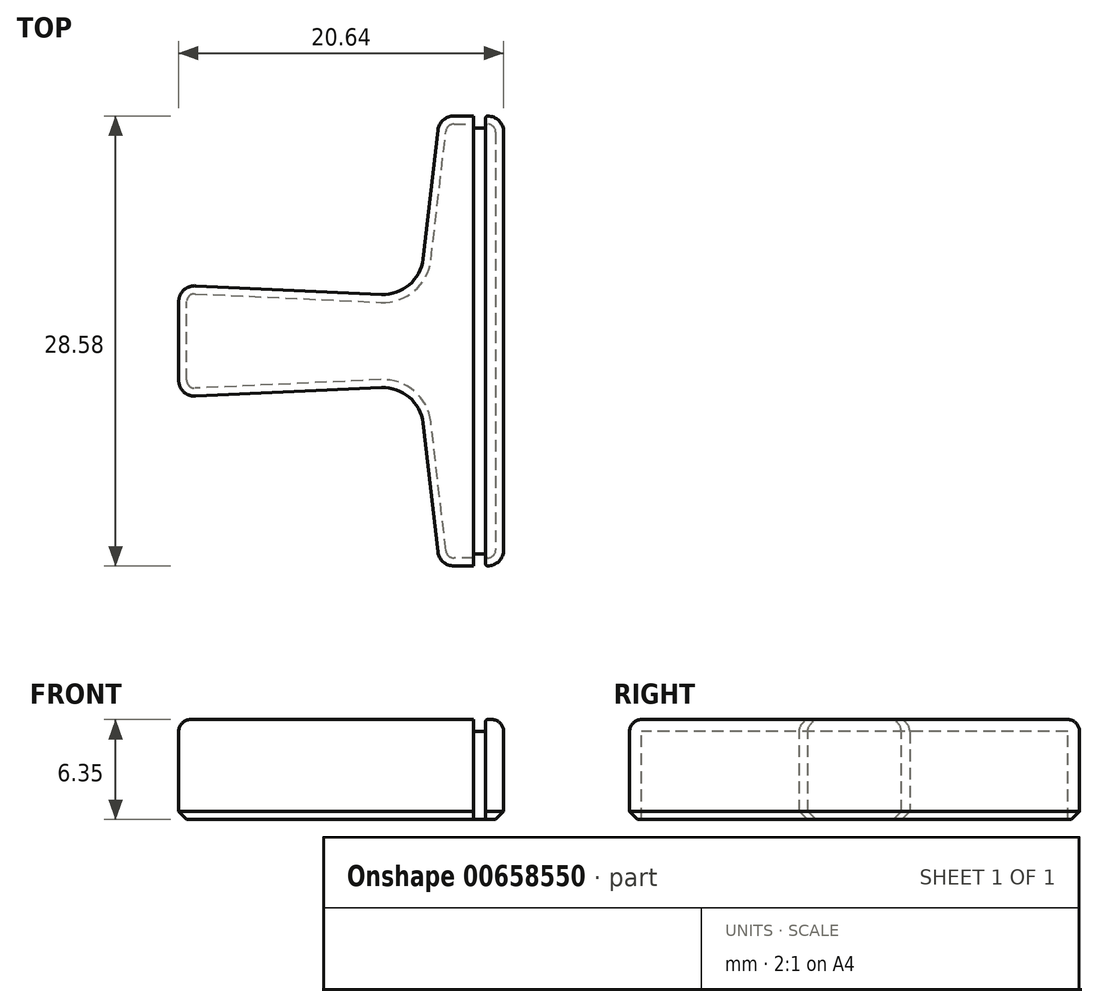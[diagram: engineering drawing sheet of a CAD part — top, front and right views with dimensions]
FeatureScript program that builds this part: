
annotation { "Feature Type Name" : "Feature", "Feature Type Description" : "" }
export const myFeature = defineFeature(function(context is Context, id is Id, definition is map)
    precondition{}
    {
        {
            var Q0;
            Q0=qCreatedBy(makeId("Top.planeOp"),FACE);
            var sketch = newSketch(context, id + "F0", { "sketchPlane" : qUnion([Q0])});
            skLineSegment(sketch, "E0", {"start": v(0, 14.29) * mm, "end": v(0, -14.29) * mm});
            skLineSegment(sketch, "E1", {"start": v(-20.64, 3.56) * mm, "end": v(-20.64, -3.56) * mm});
            skLineSegment(sketch, "E2", {"start": v(0, 14.29) * mm, "end": v(-4.06, 14.29) * mm});
            skLineSegment(sketch, "E3", {"start": v(-4.06, 14.29) * mm, "end": v(-5.4, 2.86) * mm});
            skLineSegment(sketch, "E4", {"start": v(-5.4, 2.86) * mm, "end": v(-20.64, 3.56) * mm});
            skLineSegment(sketch, "E5", {"start": v(0, -14.29) * mm, "end": v(-4.06, -14.29) * mm});
            skLineSegment(sketch, "E6", {"start": v(-4.06, -14.29) * mm, "end": v(-5.4, -2.86) * mm});
            skLineSegment(sketch, "E7", {"start": v(-5.4, -2.86) * mm, "end": v(-20.64, -3.56) * mm});
            skSolve(sketch);
        }
        {
            var Q0;
            Q0 = qSketchRegion(id + "F0", true);
            extrude(context, id + "F1", {"entities" : qUnion([Q0]), "depth" : 6.35 * mm, "offsetDistance" : 25.4 * mm});
        }
        {
            var Q0;
            Q0=makeQuery(id+"F1.opExtrude","SWEPT_EDGE",EDGE,{"disambiguationData":[OSD([sQuery(id+"F0.wireOp",EDGE,"E6"),sQuery(id+"F0.wireOp",EDGE,"E7")])]});
            var Q1;
            Q1=makeQuery(id+"F1.opExtrude","SWEPT_EDGE",EDGE,{"disambiguationData":[OSD([sQuery(id+"F0.wireOp",EDGE,"E3"),sQuery(id+"F0.wireOp",EDGE,"E4")])]});
            fillet(context, id + "F2", {"entities" : qUnion([Q0, Q1]), "radius" : 2.54 * mm, "tangentPropagation" : true, "allowEdgeOverflow" : false});
        }
        {
            var Q0;
            Q0=makeQuery(id+"F1.opExtrude","SWEPT_EDGE",EDGE,{"disambiguationData":[OSD([sQuery(id+"F0.wireOp",EDGE,"E0"),sQuery(id+"F0.wireOp",EDGE,"E2")])]});
            var Q1;
            Q1=makeQuery(id+"F1.opExtrude","SWEPT_EDGE",EDGE,{"disambiguationData":[OSD([sQuery(id+"F0.wireOp",EDGE,"E2"),sQuery(id+"F0.wireOp",EDGE,"E3")])]});
            var Q2;
            Q2=makeQuery(id+"F1.opExtrude","SWEPT_EDGE",EDGE,{"disambiguationData":[OSD([sQuery(id+"F0.wireOp",EDGE,"E0"),sQuery(id+"F0.wireOp",EDGE,"E5")])]});
            var Q3;
            Q3=makeQuery(id+"F1.opExtrude","SWEPT_EDGE",EDGE,{"disambiguationData":[OSD([sQuery(id+"F0.wireOp",EDGE,"E5"),sQuery(id+"F0.wireOp",EDGE,"E6")])]});
            var Q4;
            Q4=makeQuery(id+"F1.opExtrude","SWEPT_EDGE",EDGE,{"disambiguationData":[OSD([sQuery(id+"F0.wireOp",EDGE,"E1"),sQuery(id+"F0.wireOp",EDGE,"E4")])]});
            var Q5;
            Q5=makeQuery(id+"F1.opExtrude","SWEPT_EDGE",EDGE,{"disambiguationData":[OSD([sQuery(id+"F0.wireOp",EDGE,"E1"),sQuery(id+"F0.wireOp",EDGE,"E7")])]});
            fillet(context, id + "F3", {"entities" : qUnion([Q0, Q1, Q2, Q3, Q4, Q5]), "radius" : 1.02 * mm, "tangentPropagation" : true, "allowEdgeOverflow" : false});
        }
        {
            var Q0;
            Q0=makeQuery(id+"F1.opExtrude","CAP_FACE",FACE,{"disambiguationData":[OSD([sQuery(id+"F0.wireOp",EDGE,"E0"),sQuery(id+"F0.wireOp",EDGE,"E1"),sQuery(id+"F0.wireOp",EDGE,"E2"),sQuery(id+"F0.wireOp",EDGE,"E3"),sQuery(id+"F0.wireOp",EDGE,"E4"),sQuery(id+"F0.wireOp",EDGE,"E5"),sQuery(id+"F0.wireOp",EDGE,"E6"),sQuery(id+"F0.wireOp",EDGE,"E7")])],"isStart":false});
            fillet(context, id + "F4", {"entities" : qUnion([Q0]), "radius" : 0.76 * mm, "tangentPropagation" : true, "allowEdgeOverflow" : false});
        }
        {
            var Q0;
            Q0=makeQuery(id+"F1.opExtrude","CAP_FACE",FACE,{"disambiguationData":[OSD([sQuery(id+"F0.wireOp",EDGE,"E0"),sQuery(id+"F0.wireOp",EDGE,"E1"),sQuery(id+"F0.wireOp",EDGE,"E2"),sQuery(id+"F0.wireOp",EDGE,"E3"),sQuery(id+"F0.wireOp",EDGE,"E4"),sQuery(id+"F0.wireOp",EDGE,"E5"),sQuery(id+"F0.wireOp",EDGE,"E6"),sQuery(id+"F0.wireOp",EDGE,"E7")])],"isStart":true});
            chamfer(context, id + "F5", {"entities" : qUnion([Q0]), "width" : 0.5 * mm, "tangentPropagation" : true});
        }
        {
            var Q0;
            Q0=makeQuery(id+"F1.opExtrude","CAP_FACE",FACE,{"disambiguationData":[OSD([sQuery(id+"F0.wireOp",EDGE,"E0"),sQuery(id+"F0.wireOp",EDGE,"E1"),sQuery(id+"F0.wireOp",EDGE,"E2"),sQuery(id+"F0.wireOp",EDGE,"E3"),sQuery(id+"F0.wireOp",EDGE,"E4"),sQuery(id+"F0.wireOp",EDGE,"E5"),sQuery(id+"F0.wireOp",EDGE,"E6"),sQuery(id+"F0.wireOp",EDGE,"E7")])],"isStart":false});
            var sketch = newSketch(context, id + "F6", { "sketchPlane" : qUnion([Q0])});
            skLineSegment(sketch, "E8.bottom", {"start": v(-1.9, 15.3) * mm, "end": v(-1.14, 15.3) * mm});
            skLineSegment(sketch, "E8.top", {"start": v(-1.9, -16.46) * mm, "end": v(-1.14, -16.46) * mm});
            skLineSegment(sketch, "E8.left", {"start": v(-1.9, 15.3) * mm, "end": v(-1.9, -16.46) * mm});
            skLineSegment(sketch, "E8.right", {"start": v(-1.14, 15.3) * mm, "end": v(-1.14, -16.46) * mm});
            skSolve(sketch);
        }
        {
            var Q0;
            Q0 = qSketchRegion(id + "F6", true);
            extrude(context, id + "F7", {"entities" : qUnion([Q0]), "operationType" : NewBodyOperationType.REMOVE, "oppositeDirection" : true, "depth" : 0.76 * mm, "offsetDistance" : 25.4 * mm});
        }
        {
            var Q0;
            Q0=makeQuery(id+"F7.boolean.opBoolean","COPY",FACE,{"derivedFrom":makeQuery(id+"F7.opExtrude","CAP_FACE",FACE,{"disambiguationData":[OSD([sQuery(id+"F6.wireOp",EDGE,"E8.bottom"),sQuery(id+"F6.wireOp",EDGE,"E8.top"),sQuery(id+"F6.wireOp",EDGE,"E8.left"),sQuery(id+"F6.wireOp",EDGE,"E8.right")])],"isStart":false})});
            var sketch = newSketch(context, id + "F8", { "sketchPlane" : qUnion([Q0])});
            skLineSegment(sketch, "E9.bottom", {"start": v(-1.9, 14.29) * mm, "end": v(-1.14, 14.29) * mm});
            skLineSegment(sketch, "E9.top", {"start": v(-1.9, 13.54) * mm, "end": v(-1.14, 13.54) * mm});
            skLineSegment(sketch, "E9.left", {"start": v(-1.9, 14.29) * mm, "end": v(-1.9, 13.54) * mm});
            skLineSegment(sketch, "E9.right", {"start": v(-1.14, 14.29) * mm, "end": v(-1.14, 13.54) * mm});
            skLineSegment(sketch, "E10.bottom", {"start": v(-1.14, -14.29) * mm, "end": v(-1.9, -14.29) * mm});
            skLineSegment(sketch, "E10.top", {"start": v(-1.14, -13.53) * mm, "end": v(-1.9, -13.53) * mm});
            skLineSegment(sketch, "E10.left", {"start": v(-1.14, -14.29) * mm, "end": v(-1.14, -13.53) * mm});
            skLineSegment(sketch, "E10.right", {"start": v(-1.9, -14.29) * mm, "end": v(-1.9, -13.53) * mm});
            skSolve(sketch);
        }
        {
            var Q0;
            Q0 = qSketchRegion(id + "F8", true);
            extrude(context, id + "F9", {"entities" : qUnion([Q0]), "operationType" : NewBodyOperationType.REMOVE, "oppositeDirection" : true, "depth" : 25.4 * mm, "offsetDistance" : 25.4 * mm});
        }
        {
            var Q0;
            Q0=makeQuery(id+"F7.boolean.opBoolean","COPY",EDGE,{"derivedFrom":makeQuery(id+"F7.opExtrude","CAP_EDGE",EDGE,{"disambiguationData":[OSD([sQuery(id+"F6.wireOp",EDGE,"E8.right")])],"isStart":true})});
            var Q1;
            Q1=makeQuery(id+"F7.boolean.opBoolean","COPY",EDGE,{"derivedFrom":makeQuery(id+"F7.opExtrude","CAP_EDGE",EDGE,{"disambiguationData":[OSD([sQuery(id+"F6.wireOp",EDGE,"E8.left")])],"isStart":true})});
            fillet(context, id + "F10", {"entities" : qUnion([Q0, Q1]), "radius" : 0.13 * mm, "tangentPropagation" : true, "allowEdgeOverflow" : false});
        }
    });
